# Revit family: QSC Q-SYS NV-32-H_Surface Mount
name_source: partatom
category: Generic Models
revit_build: Autodesk Revit 2017 (Build: 20190508_0315(x64)
units: mm (PartAtom-declared; Revit-internal decimal feet)

## family parameters
Can host rebar = No
Cut with Voids When Loaded = No
Host = Face
Part Type = Normal
Room Calculation Point = No
Round Connector Dimension = Use Diameter
Shared = No

## types (1)
- NV-32-H
    Default Elevation = 0.000"
    Depth = 11.280"
    Description = Network Video Endpoint for the Q-SYS Ecosystem
    Face Depth = 0.079"
    Height = 1.720"
    Manufacturer = QSC
    Manufacturer URL = http://www.qsc.com
    Model = Q-SYS NV-32-H
    Operating Temperature Max = 50C
    Operating Temperature Min = 0C
    Product Documentation Link = https://www.qsc.com
    Product Page URL = https://www.qsc.com
    Regulatory Compliance = CE, FCC Part 15 Class B, RoHS
    Voltage DC = 48
    Weight Product (kg) = 1.81
    Weight Product (lb) = 4
    Width = 8.660"

## geometry (parser evidence)
native form markers: Blend x2, Sweep x3
no freeform markers — native parametric forms only
